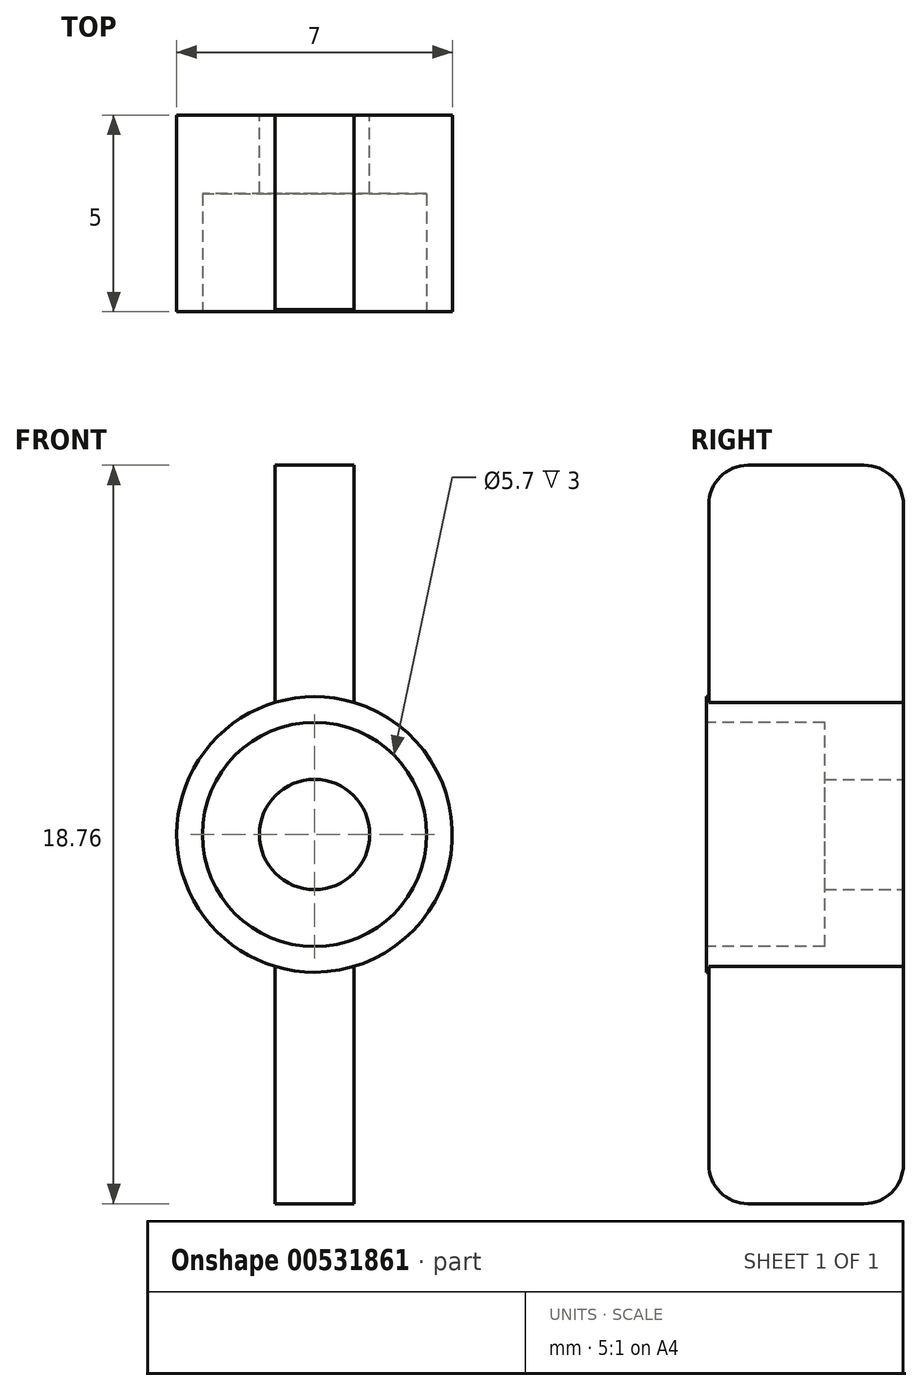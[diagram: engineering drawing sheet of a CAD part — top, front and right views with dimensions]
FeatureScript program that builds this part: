
annotation { "Feature Type Name" : "Feature", "Feature Type Description" : "" }
export const myFeature = defineFeature(function(context is Context, id is Id, definition is map)
    precondition{}
    {
        {
            var Q0;
            Q0=qCreatedBy(makeId("Front.planeOp"),FACE);
            var sketch = newSketch(context, id + "F0", { "sketchPlane" : qUnion([Q0])});
            skCircle(sketch, "E0", {"center": v(0, 0) * mm, "radius": 1.4 * mm});
            skCircle(sketch, "E1", {"center": v(0, 0) * mm, "radius": 3.5 * mm});
            skSolve(sketch);
        }
        {
            var Q0;
            Q0=qSketchRegion(id+"F0",true);
            extrude(context, id + "F1", {"entities" : qUnion([Q0]), "depth" : 5 * mm});
        }
        {
            var Q0;
            Q0=makeQuery(id+"F1.opExtrude","CAP_FACE",FACE,{"disambiguationData":[OSD([sQuery(id+"F0.wireOp",EDGE,"E0"),sQuery(id+"F0.wireOp",EDGE,"E1")])],"isStart":false});
            var sketch = newSketch(context, id + "F2", { "sketchPlane" : qUnion([Q0])});
            skCircle(sketch, "E2", {"center": v(0, 0) * mm, "radius": 2.85 * mm});
            skSolve(sketch);
        }
        {
            var Q0;
            Q0=qCreatedBy(makeId("Right.planeOp"),FACE);
            var sketch = newSketch(context, id + "F3", { "sketchPlane" : qUnion([Q0])});
            skLineSegment(sketch, "E3", {"start": v(0, 0) * mm, "end": v(0, -3.5) * mm});
            skLineSegment(sketch, "E4", {"start": v(0, -9.38) * mm, "end": v(0, -3.5) * mm});
            skPoint(sketch, "E5.visualSharp", {"position": v(-8.54, -11.09) * mm});
            skPoint(sketch, "E6.visualSharp", {"position": v(0, -11.09) * mm});
            skPoint(sketch, "E7.oppositeSnap0", {"position": v(0, -1.75) * mm});
            skLineSegment(sketch, "E7.top", {"start": v(0, -1.75) * mm, "end": v(-4.95, -1.75) * mm});
            skLineSegment(sketch, "E7.left", {"start": v(0, -3.5) * mm, "end": v(0, -1.75) * mm});
            skLineSegment(sketch, "E7.right", {"start": v(-4.95, -3.5) * mm, "end": v(-4.95, -1.75) * mm});
            skLineSegment(sketch, "E8", {"start": v(-4.95, -3.38) * mm, "end": v(-4.95, -9.38) * mm});
            skLineSegment(sketch, "E9", {"start": v(-4.95, -9.38) * mm, "end": v(0, -9.38) * mm});
            skPoint(sketch, "E5.filletArc.start.orphan", {"position": v(-8, -9.95) * mm});
            skPoint(sketch, "E10.start.orphan", {"position": v(-7.28, -11.09) * mm});
            skPoint(sketch, "E6.filletArc.start.orphan", {"position": v(-0.8, -11.09) * mm});
            skPoint(sketch, "E11.orphan", {"position": v(0, -10.29) * mm});
            skLineSegment(sketch, "E12", {"start": v(0, 0) * mm, "end": v(2.3, 0) * mm});
            skLineSegment(sketch, "E13.MirrorCS", {"start": v(0, 0) * mm, "end": v(0, 3.5) * mm});
            skLineSegment(sketch, "E14.MirrorCS", {"start": v(0, 3.5) * mm, "end": v(0, 1.75) * mm});
            skLineSegment(sketch, "E15.MirrorCS", {"start": v(-4.95, 3.5) * mm, "end": v(-4.95, 1.75) * mm});
            skPoint(sketch, "E16.MirrorP", {"position": v(0, 10.29) * mm});
            skLineSegment(sketch, "E17.MirrorCS", {"start": v(0, 1.75) * mm, "end": v(-4.95, 1.75) * mm});
            skPoint(sketch, "E18.MirrorP", {"position": v(0, 1.75) * mm});
            skLineSegment(sketch, "E19.MirrorCS", {"start": v(-4.95, 9.38) * mm, "end": v(0, 9.38) * mm});
            skLineSegment(sketch, "E20.MirrorCS", {"start": v(-4.95, 3.38) * mm, "end": v(-4.95, 9.38) * mm});
            skLineSegment(sketch, "E21.MirrorCS", {"start": v(0, 9.38) * mm, "end": v(0, 3.5) * mm});
            skSolve(sketch);
        }
        {
            var Q0;
            Q0=qSketchRegion(id+"F3",true);
            extrude(context, id + "F4", {"entities" : qUnion([Q0]), "operationType" : NewBodyOperationType.ADD, "endBound" : BoundingType.SYMMETRIC, "depth" : 2 * mm});
        }
        {
            var Q0;
            Q0=qSketchRegion(id+"F2",true);
            extrude(context, id + "F5", {"entities" : qUnion([Q0]), "operationType" : NewBodyOperationType.REMOVE, "oppositeDirection" : true, "depth" : 3 * mm});
        }
        {
            var Q0;
            Q0=makeQuery(id+"F4.opExtrude","SWEPT_EDGE",EDGE,{"disambiguationData":[OSD([sQuery(id+"F3.wireOp",EDGE,"E19.MirrorCS"),sQuery(id+"F3.wireOp",EDGE,"E20.MirrorCS")])]});
            var Q1;
            Q1=makeQuery(id+"F4.opExtrude","SWEPT_EDGE",EDGE,{"disambiguationData":[OSD([sQuery(id+"F3.wireOp",EDGE,"E19.MirrorCS"),sQuery(id+"F3.wireOp",EDGE,"E21.MirrorCS")])]});
            var Q2;
            Q2=makeQuery(id+"F4.opExtrude","SWEPT_EDGE",EDGE,{"disambiguationData":[OSD([sQuery(id+"F3.wireOp",EDGE,"E8"),sQuery(id+"F3.wireOp",EDGE,"E9")])]});
            var Q3;
            Q3=makeQuery(id+"F4.opExtrude","SWEPT_EDGE",EDGE,{"disambiguationData":[OSD([sQuery(id+"F3.wireOp",EDGE,"E4"),sQuery(id+"F3.wireOp",EDGE,"E9")])]});
            fillet(context, id + "F6", {"entities" : qUnion([Q0, Q1, Q2, Q3]), "radius" : 1 * mm, "tangentPropagation" : true, "allowEdgeOverflow" : false});
        }
    });
